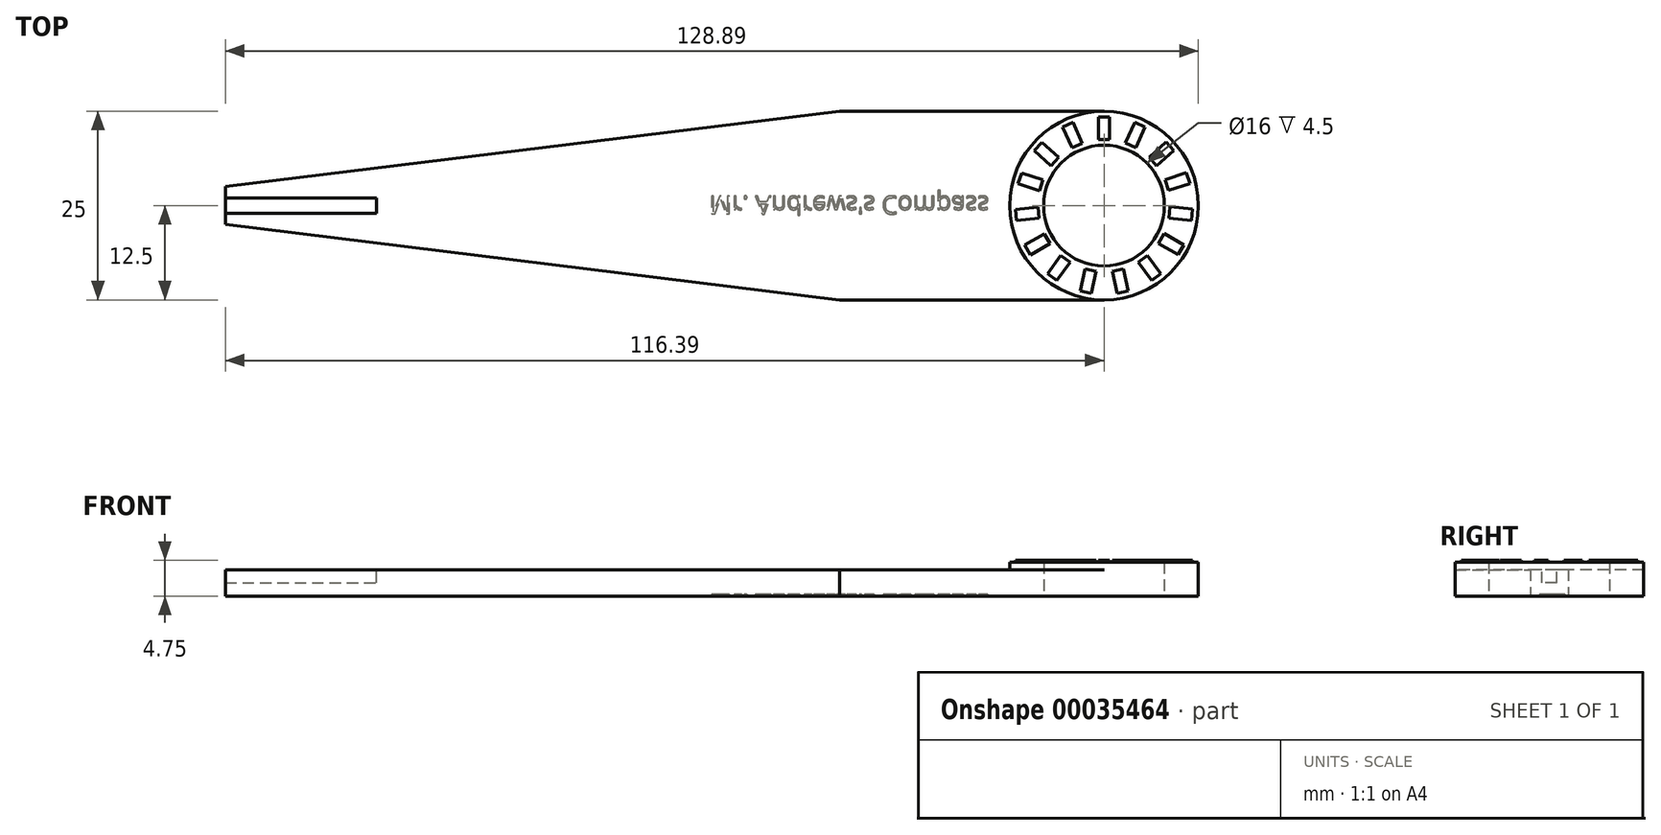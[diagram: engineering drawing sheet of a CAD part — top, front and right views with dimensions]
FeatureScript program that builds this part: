
annotation { "Feature Type Name" : "Feature", "Feature Type Description" : "" }
export const myFeature = defineFeature(function(context is Context, id is Id, definition is map)
    precondition{}
    {
        {
            var Q0;
            Q0=qCreatedBy(makeId("Top.planeOp"),FACE);
            var sketch = newSketch(context, id + "F0", { "sketchPlane" : qUnion([Q0])});
            skCircle(sketch, "E0", {"center": v(0, 0) * mm, "radius": 8 * mm});
            skCircle(sketch, "E1", {"center": v(0, 0) * mm, "radius": 12.5 * mm});
            skLineSegment(sketch, "E2", {"start": v(-35, 12.5) * mm, "end": v(0, 12.5) * mm});
            skLineSegment(sketch, "E3", {"start": v(-35, -12.5) * mm, "end": v(0, -12.5) * mm});
            skLineSegment(sketch, "E4", {"start": v(-35, 12.5) * mm, "end": v(-93.64, 12.5) * mm, "construction": true});
            skLineSegment(sketch, "E5", {"start": v(-35, 12.5) * mm, "end": v(-116.39, 2.5) * mm});
            skLineSegment(sketch, "E6", {"start": v(-35, -12.5) * mm, "end": v(-94.55, -12.5) * mm, "construction": true});
            skLineSegment(sketch, "E7", {"start": v(-35, -12.5) * mm, "end": v(-116.39, -2.5) * mm});
            skLineSegment(sketch, "E8", {"start": v(-116.39, 2.5) * mm, "end": v(-116.39, -2.5) * mm});
            skSolve(sketch);
        }
        {
            var Q0;
            Q0 = qSketchRegion(id + "F0", true);
            extrude(context, id + "F1", {"entities" : qUnion([Q0]), "depth" : 3.5 * mm});
        }
        {
            var Q0;
            Q0=makeQuery(id+"F1.opExtrude","CAP_FACE",FACE,{"disambiguationData":[OSD([sQuery(id+"F0.wireOp",EDGE,"E0"),sQuery(id+"F0.wireOp",EDGE,"E1"),sQuery(id+"F0.wireOp",EDGE,"E2"),sQuery(id+"F0.wireOp",EDGE,"E3"),sQuery(id+"F0.wireOp",EDGE,"E5"),sQuery(id+"F0.wireOp",EDGE,"E7"),sQuery(id+"F0.wireOp",EDGE,"E8")])],"isStart":false});
            var sketch = newSketch(context, id + "F2", { "sketchPlane" : qUnion([Q0])});
            skCircle(sketch, "E9", {"center": v(0, 0) * mm, "radius": 12.5 * mm});
            skCircle(sketch, "E10", {"center": v(0, 0) * mm, "radius": 8 * mm});
            skSolve(sketch);
        }
        {
            var Q0;
            Q0 = qSketchRegion(id + "F2", true);
            extrude(context, id + "F3", {"entities" : qUnion([Q0]), "operationType" : NewBodyOperationType.ADD, "depth" : 1 * mm});
        }
        {
            var Q0;
            Q0=makeQuery(id+"F1.opExtrude","CAP_FACE",FACE,{"disambiguationData":[OSD([sQuery(id+"F0.wireOp",EDGE,"E0"),sQuery(id+"F0.wireOp",EDGE,"E1"),sQuery(id+"F0.wireOp",EDGE,"E2"),sQuery(id+"F0.wireOp",EDGE,"E3"),sQuery(id+"F0.wireOp",EDGE,"E5"),sQuery(id+"F0.wireOp",EDGE,"E7"),sQuery(id+"F0.wireOp",EDGE,"E8")])],"isStart":false});
            var sketch = newSketch(context, id + "F4", { "sketchPlane" : qUnion([Q0])});
            skLineSegment(sketch, "E11.bottom", {"start": v(-116.39, 1) * mm, "end": v(-96.39, 1) * mm});
            skLineSegment(sketch, "E11.top", {"start": v(-116.39, -1) * mm, "end": v(-96.39, -1) * mm});
            skLineSegment(sketch, "E11.left", {"start": v(-116.39, 1) * mm, "end": v(-116.39, -1) * mm});
            skLineSegment(sketch, "E11.right", {"start": v(-96.39, 1) * mm, "end": v(-96.39, -1) * mm});
            skSolve(sketch);
        }
        {
            var Q0;
            Q0 = qSketchRegion(id + "F4", true);
            extrude(context, id + "F5", {"entities" : qUnion([Q0]), "operationType" : NewBodyOperationType.REMOVE, "oppositeDirection" : true, "depth" : 1.75 * mm});
        }
        {
            var Q0;
            Q0=makeQuery(id+"F3.opExtrude","CAP_FACE",FACE,{"disambiguationData":[OSD([sQuery(id+"F2.wireOp",EDGE,"E9"),sQuery(id+"F2.wireOp",EDGE,"E10")])],"isStart":false});
            var sketch = newSketch(context, id + "F6", { "sketchPlane" : qUnion([Q0])});
            skLineSegment(sketch, "E12.bottom", {"start": v(-0.77, 11.73) * mm, "end": v(0.73, 11.73) * mm});
            skLineSegment(sketch, "E12.top", {"start": v(-0.77, 8.73) * mm, "end": v(0.73, 8.73) * mm});
            skLineSegment(sketch, "E12.left", {"start": v(-0.77, 11.73) * mm, "end": v(-0.77, 8.73) * mm});
            skLineSegment(sketch, "E12.right", {"start": v(0.73, 11.73) * mm, "end": v(0.73, 8.73) * mm});
            skLineSegment(sketch, "E13.1.0", {"start": v(-5.47, 10.4) * mm, "end": v(-4.25, 7.66) * mm});
            skLineSegment(sketch, "E13.1.1", {"start": v(-5.47, 10.4) * mm, "end": v(-4.1, 11.01) * mm});
            skLineSegment(sketch, "E13.1.2", {"start": v(-4.1, 11.01) * mm, "end": v(-2.88, 8.27) * mm});
            skLineSegment(sketch, "E13.1.3", {"start": v(-4.25, 7.66) * mm, "end": v(-2.88, 8.27) * mm});
            skLineSegment(sketch, "E13.2.0", {"start": v(-9.23, 7.28) * mm, "end": v(-7, 5.27) * mm});
            skLineSegment(sketch, "E13.2.1", {"start": v(-9.23, 7.28) * mm, "end": v(-8.22, 8.4) * mm});
            skLineSegment(sketch, "E13.2.2", {"start": v(-8.22, 8.4) * mm, "end": v(-6, 6.38) * mm});
            skLineSegment(sketch, "E13.2.3", {"start": v(-7, 5.27) * mm, "end": v(-6, 6.38) * mm});
            skLineSegment(sketch, "E13.3.0", {"start": v(-11.39, 2.9) * mm, "end": v(-8.53, 1.97) * mm});
            skLineSegment(sketch, "E13.3.1", {"start": v(-11.39, 2.9) * mm, "end": v(-10.92, 4.32) * mm});
            skLineSegment(sketch, "E13.3.2", {"start": v(-10.92, 4.32) * mm, "end": v(-8.07, 3.4) * mm});
            skLineSegment(sketch, "E13.3.3", {"start": v(-8.53, 1.97) * mm, "end": v(-8.07, 3.4) * mm});
            skLineSegment(sketch, "E13.4.0", {"start": v(-11.58, -1.99) * mm, "end": v(-8.6, -1.67) * mm});
            skLineSegment(sketch, "E13.4.1", {"start": v(-11.58, -1.99) * mm, "end": v(-11.74, -0.5) * mm});
            skLineSegment(sketch, "E13.4.2", {"start": v(-11.74, -0.5) * mm, "end": v(-8.75, -0.18) * mm});
            skLineSegment(sketch, "E13.4.3", {"start": v(-8.6, -1.67) * mm, "end": v(-8.75, -0.18) * mm});
            skLineSegment(sketch, "E13.5.0", {"start": v(-9.77, -6.53) * mm, "end": v(-7.17, -5.03) * mm});
            skLineSegment(sketch, "E13.5.1", {"start": v(-9.77, -6.53) * mm, "end": v(-10.52, -5.23) * mm});
            skLineSegment(sketch, "E13.5.2", {"start": v(-10.52, -5.23) * mm, "end": v(-7.92, -3.73) * mm});
            skLineSegment(sketch, "E13.5.3", {"start": v(-7.17, -5.03) * mm, "end": v(-7.92, -3.73) * mm});
            skLineSegment(sketch, "E13.6.0", {"start": v(-6.27, -9.94) * mm, "end": v(-4.5, -7.5) * mm});
            skLineSegment(sketch, "E13.6.1", {"start": v(-6.27, -9.94) * mm, "end": v(-7.49, -9.05) * mm});
            skLineSegment(sketch, "E13.6.2", {"start": v(-7.49, -9.05) * mm, "end": v(-5.72, -6.63) * mm});
            skLineSegment(sketch, "E13.6.3", {"start": v(-4.5, -7.5) * mm, "end": v(-5.72, -6.63) * mm});
            skLineSegment(sketch, "E13.7.0", {"start": v(-1.69, -11.63) * mm, "end": v(-1.07, -8.7) * mm});
            skLineSegment(sketch, "E13.7.1", {"start": v(-1.69, -11.63) * mm, "end": v(-3.16, -11.32) * mm});
            skLineSegment(sketch, "E13.7.2", {"start": v(-3.16, -11.32) * mm, "end": v(-2.53, -8.38) * mm});
            skLineSegment(sketch, "E13.7.3", {"start": v(-1.07, -8.7) * mm, "end": v(-2.53, -8.38) * mm});
            skLineSegment(sketch, "E13.8.0", {"start": v(3.19, -11.3) * mm, "end": v(2.56, -8.38) * mm});
            skLineSegment(sketch, "E13.8.1", {"start": v(3.19, -11.3) * mm, "end": v(1.72, -11.62) * mm});
            skLineSegment(sketch, "E13.8.2", {"start": v(1.72, -11.62) * mm, "end": v(1.1, -8.69) * mm});
            skLineSegment(sketch, "E13.8.3", {"start": v(2.56, -8.38) * mm, "end": v(1.1, -8.69) * mm});
            skLineSegment(sketch, "E13.9.0", {"start": v(7.51, -9.04) * mm, "end": v(5.75, -6.6) * mm});
            skLineSegment(sketch, "E13.9.1", {"start": v(7.51, -9.04) * mm, "end": v(6.3, -9.92) * mm});
            skLineSegment(sketch, "E13.9.2", {"start": v(6.3, -9.92) * mm, "end": v(4.53, -7.5) * mm});
            skLineSegment(sketch, "E13.9.3", {"start": v(5.75, -6.6) * mm, "end": v(4.53, -7.5) * mm});
            skLineSegment(sketch, "E13.10.0", {"start": v(10.54, -5.2) * mm, "end": v(7.94, -3.7) * mm});
            skLineSegment(sketch, "E13.10.1", {"start": v(10.54, -5.2) * mm, "end": v(9.79, -6.5) * mm});
            skLineSegment(sketch, "E13.10.2", {"start": v(9.79, -6.5) * mm, "end": v(7.19, -5) * mm});
            skLineSegment(sketch, "E13.10.3", {"start": v(7.94, -3.7) * mm, "end": v(7.19, -5) * mm});
            skLineSegment(sketch, "E13.11.0", {"start": v(11.74, -0.46) * mm, "end": v(8.76, -0.15) * mm});
            skLineSegment(sketch, "E13.11.1", {"start": v(11.74, -0.46) * mm, "end": v(11.58, -1.96) * mm});
            skLineSegment(sketch, "E13.11.2", {"start": v(11.58, -1.96) * mm, "end": v(8.6, -1.64) * mm});
            skLineSegment(sketch, "E13.11.3", {"start": v(8.76, -0.15) * mm, "end": v(8.6, -1.64) * mm});
            skLineSegment(sketch, "E13.12.0", {"start": v(10.91, 4.35) * mm, "end": v(8.06, 3.42) * mm});
            skLineSegment(sketch, "E13.12.1", {"start": v(10.91, 4.35) * mm, "end": v(11.38, 2.92) * mm});
            skLineSegment(sketch, "E13.12.2", {"start": v(11.38, 2.92) * mm, "end": v(8.53, 2) * mm});
            skLineSegment(sketch, "E13.12.3", {"start": v(8.06, 3.42) * mm, "end": v(8.53, 2) * mm});
            skLineSegment(sketch, "E13.13.0", {"start": v(8.2, 8.41) * mm, "end": v(5.97, 6.4) * mm});
            skLineSegment(sketch, "E13.13.1", {"start": v(8.2, 8.41) * mm, "end": v(9.2, 7.3) * mm});
            skLineSegment(sketch, "E13.13.2", {"start": v(9.2, 7.3) * mm, "end": v(6.98, 5.3) * mm});
            skLineSegment(sketch, "E13.13.3", {"start": v(5.97, 6.4) * mm, "end": v(6.98, 5.3) * mm});
            skLineSegment(sketch, "E13.14.0", {"start": v(4.07, 11.02) * mm, "end": v(2.85, 8.28) * mm});
            skLineSegment(sketch, "E13.14.1", {"start": v(4.07, 11.02) * mm, "end": v(5.44, 10.41) * mm});
            skLineSegment(sketch, "E13.14.2", {"start": v(5.44, 10.41) * mm, "end": v(4.22, 7.67) * mm});
            skLineSegment(sketch, "E13.14.3", {"start": v(2.85, 8.28) * mm, "end": v(4.22, 7.67) * mm});
            skPoint(sketch, "E13.center", {"position": v(0, 0) * mm});
            skSolve(sketch);
        }
        {
            var Q0;
            Q0 = qSketchRegion(id + "F6", true);
            extrude(context, id + "F7", {"entities" : qUnion([Q0]), "operationType" : NewBodyOperationType.ADD, "depth" : .25 * mm});
        }
        {
            var Q0;
            Q0=makeQuery(id+"F1.opExtrude","CAP_FACE",FACE,{"disambiguationData":[OSD([sQuery(id+"F0.wireOp",EDGE,"E0"),sQuery(id+"F0.wireOp",EDGE,"E1"),sQuery(id+"F0.wireOp",EDGE,"E2"),sQuery(id+"F0.wireOp",EDGE,"E3"),sQuery(id+"F0.wireOp",EDGE,"E5"),sQuery(id+"F0.wireOp",EDGE,"E7"),sQuery(id+"F0.wireOp",EDGE,"E8")])],"isStart":true});
            var sketch = newSketch(context, id + "F8", { "sketchPlane" : qUnion([Q0])});
            skText(sketch, "E14", { "text": "Mr. Andrews\'s Compass", "fontName": "OpenSans-Regular.ttf"});
            const initialGuessF8  = {"E14": [-0.05229, -0.00125, 1, 0, 0.00239]};
            skSetInitialGuess(sketch, initialGuessF8);
            skSolve(sketch);
        }
        {
            var Q0;
            Q0 = qSketchRegion(id + "F8", true);
            extrude(context, id + "F9", {"entities" : qUnion([Q0]), "operationType" : NewBodyOperationType.REMOVE, "oppositeDirection" : true, "depth" : .25 * mm});
        }
    });
